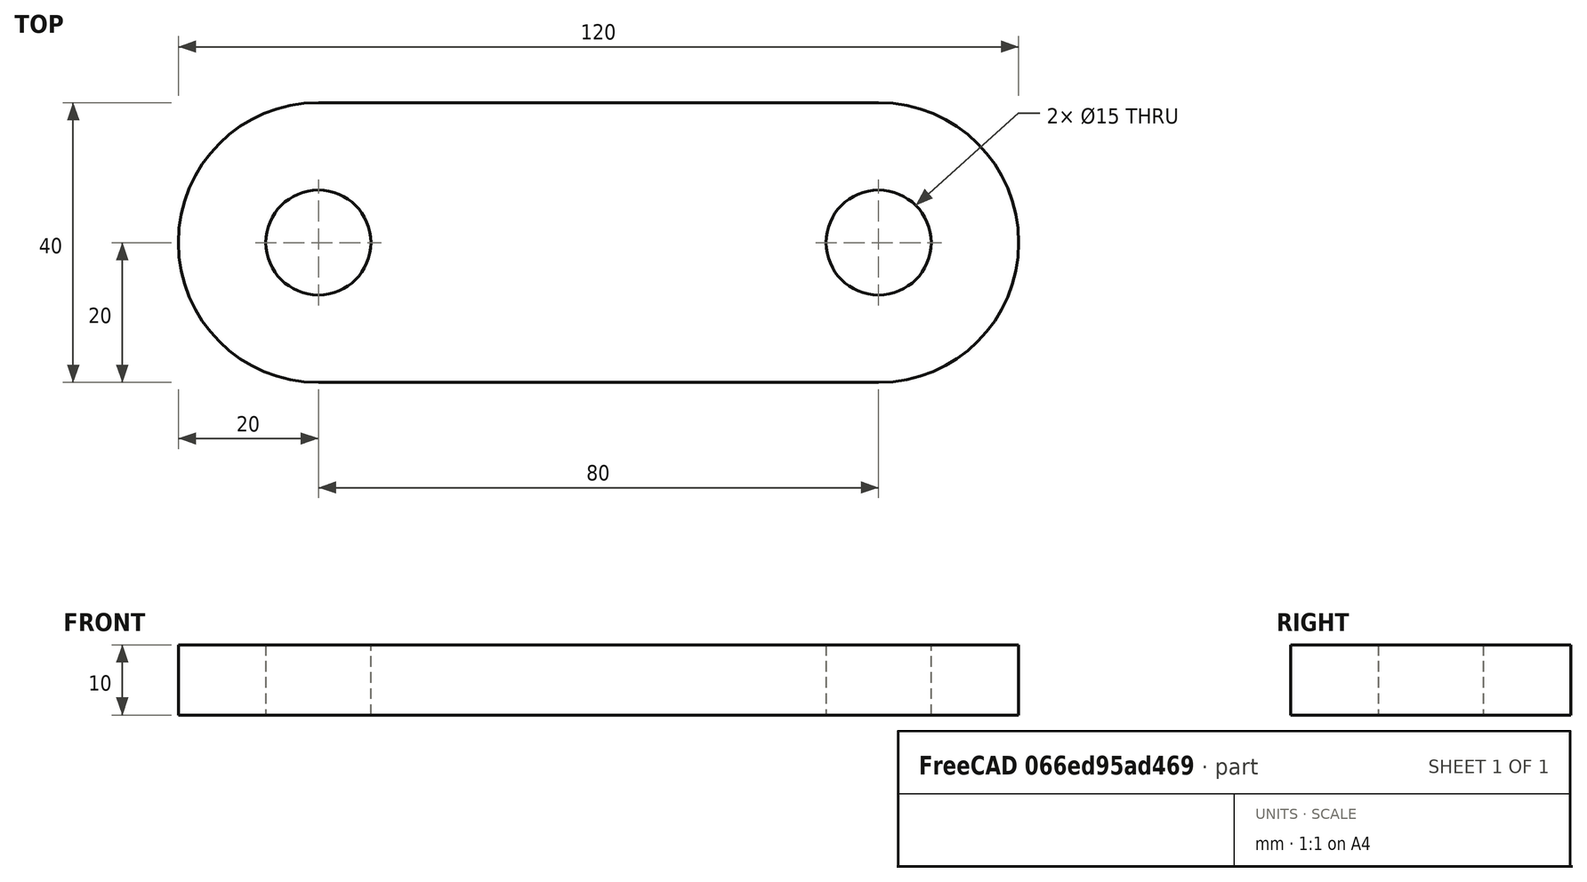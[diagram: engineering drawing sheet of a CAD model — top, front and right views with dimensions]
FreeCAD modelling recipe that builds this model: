
FCSTD DOCUMENT  (FreeCAD 0.18R16146 (Git))
Label: pieza
License: All rights reserved
LicenseURL: http://en.wikipedia.org/wiki/All_rights_reserved
objects: Sketcher::SketchObject×1, PartDesign::Pad×1, PartDesign::Body×1, App::Part×1
note: 4 computed .brp shape members not serialized (recipe doc carries the construction recipe); baked Part::Feature solids carry a one-line shape summary decoded from their .brp

FEATURE [Sketcher::SketchObject] Sketch
  MapMode = 5
  Support = -> [XY_Plane001]
  sketch-geometry (6):
    g0: LineSegment StartX=-40 StartY=20 StartZ=0 EndX=40 EndY=20 EndZ=0
    g1: ArcOfCircle CenterX=40 CenterY=-7e-16 CenterZ=0 NormalX=0 NormalY=0 NormalZ=1 AngleXU=0 Radius=20 StartAngle=4.71239 EndAngle=7.85398
    g2: LineSegment StartX=40 StartY=-20 StartZ=0 EndX=-40 EndY=-20 EndZ=0
    g3: ArcOfCircle CenterX=-40 CenterY=7e-16 CenterZ=0 NormalX=0 NormalY=0 NormalZ=1 AngleXU=0 Radius=20 StartAngle=1.5708 EndAngle=4.71239
    g4: Circle CenterX=-40 CenterY=7e-16 CenterZ=0 NormalX=0 NormalY=0 NormalZ=1 AngleXU=0 Radius=7.5
    g5: Circle CenterX=40 CenterY=-7e-16 CenterZ=0 NormalX=0 NormalY=0 NormalZ=1 AngleXU=0 Radius=7.5
  constraints (13):
    c: Tangent(g0,g1) = 1.5708
    c: Tangent(g1,g2) = 1.5708
    c: Tangent(g2,g3) = 1.5708
    c: Horizontal(g0)
    c: Horizontal(g2)
    c: Tangent(g3,g0) = 1.5708
    c: Radius(g3) = 20
    c: Equal(g4,g5)
    c: Diameter(g4) = 15
    c: DistanceX(g3,g1) = 80
    c: Coincident(g4,g3)
    c: Coincident(g5,g1)
    c: Symmetric(g3,g1,g-1)
FEATURE [PartDesign::Pad] Pad
  Length = 10
  Length2 = 100
  Profile = -> Sketch
  Type = 0
FEATURE [PartDesign::Body] Body
  Group = -> [Sketch,Pad]
  Origin = -> Origin001
  Tip = -> Pad
FEATURE [App::Part] Part  label="pieza"
  Group = -> [Body]
  Origin = -> Origin
